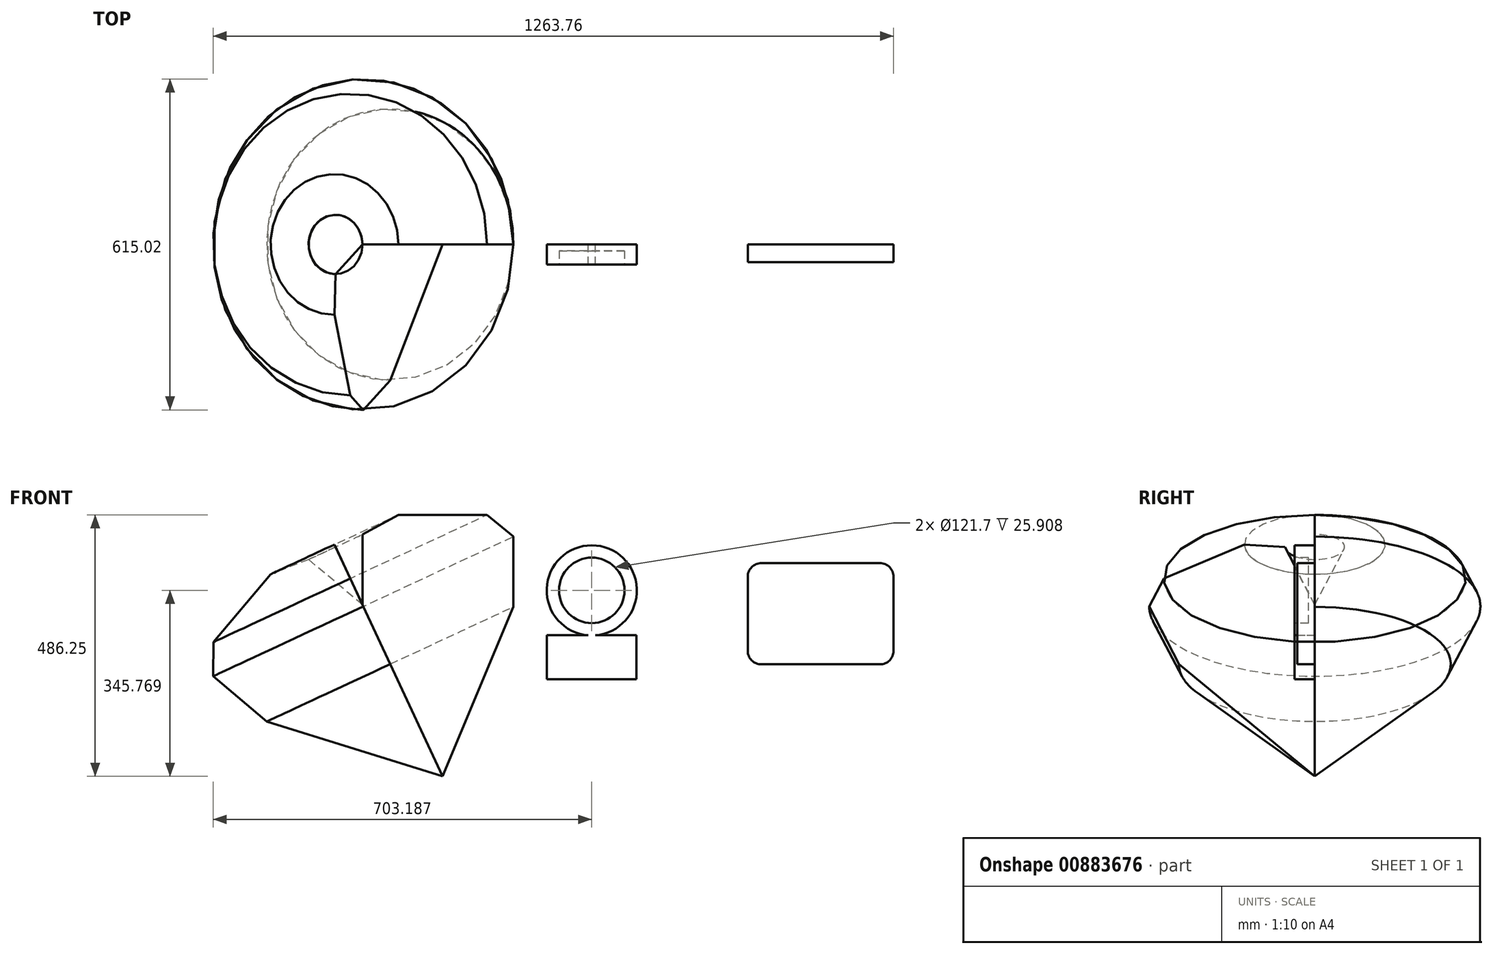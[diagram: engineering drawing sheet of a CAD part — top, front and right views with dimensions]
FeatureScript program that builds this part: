
annotation { "Feature Type Name" : "Feature", "Feature Type Description" : "" }
export const myFeature = defineFeature(function(context is Context, id is Id, definition is map)
    precondition{}
    {
        {
            var Q0;
            Q0=qCreatedBy(makeId("Front.planeOp"),FACE);
            var sketch = newSketch(context, id + "F0", { "sketchPlane" : qUnion([Q0])});
            skLineSegment(sketch, "E0.bottom", {"start": v(-289.04, 54.01) * mm, "end": v(-122.87, 54.01) * mm});
            skLineSegment(sketch, "E0.top", {"start": v(-289.04, -27.36) * mm, "end": v(-122.87, -27.36) * mm});
            skLineSegment(sketch, "E0.left", {"start": v(-289.04, 54.01) * mm, "end": v(-289.04, -27.36) * mm});
            skLineSegment(sketch, "E0.right", {"start": v(-122.87, 54.01) * mm, "end": v(-122.87, -27.36) * mm});
            skCircle(sketch, "E1", {"center": v(-205.51, 137.54) * mm, "radius": 83.78 * mm});
            skCircle(sketch, "E2", {"center": v(-205.51, 137.54) * mm, "radius": 83.53 * mm});
            skSolve(sketch);
        }
        {
            var Q0;
            Q0=makeQuery(id+"F0.imprint","IMPRINT",FACE,{"disambiguationData":[TD([[makeQuery(id+"F0.imprint","IMPRINT",EDGE,{"derivedFrom":sQuery(id+"F0.wireOp",EDGE,"E0.top")}),1.0]])]});
            var Q1;
            Q1=makeQuery(id+"F0.imprint","IMPRINT",FACE,{"disambiguationData":[TD([[makeQuery(id+"F0.imprint","IMPRINT",EDGE,{"derivedFrom":sQuery(id+"F0.wireOp",EDGE,"E2")}),1.0]])]});
            var Q2;
            {var subQ3=sQuery(id+"F0.wireOp",EDGE,"E2");Q2=makeQuery(id+"F0.imprint","IMPRINT",FACE,{"disambiguationData":[TD([[makeQuery(id+"F0.imprint","IMPRINT",EDGE,{"derivedFrom":subQ3}),-1.0]])]});}
            var Q3;
            {var subQ0=sQuery(id+"F0.wireOp",EDGE,"E1");var subQ1=sQuery(id+"F0.wireOp",EDGE,"E0.bottom");var subQ2=makeQuery(id+"F0.imprint","INTERSECT",VERTEX,{"disambiguationData":[OD(0.0)],"derivedFrom":[subQ1,subQ0]});Q3=makeQuery(id+"F0.imprint","IMPRINT",FACE,{"disambiguationData":[TD([[makeQuery(id+"F0.imprint","IMPRINT",EDGE,{"disambiguationData":[TD([[subQ2,-1.0]])],"derivedFrom":subQ1}),-1.0]])]});}
            extrude(context, id + "F1", {"entities" : qUnion([Q0, Q1, Q2, Q3]), "surfaceOperationType" : NewSurfaceOperationType.ADD, "depth" : 37.6 * mm, "offsetDistance" : 25.4 * mm});
        }
        {
            var Q0;
            Q0=makeQuery(id+"F1.opExtrude","CAP_FACE",FACE,{"disambiguationData":[OSD([sQuery(id+"F0.wireOp",EDGE,"E0.bottom"),sQuery(id+"F0.wireOp",EDGE,"E0.top"),sQuery(id+"F0.wireOp",EDGE,"E0.left"),sQuery(id+"F0.wireOp",EDGE,"E0.right"),sQuery(id+"F0.wireOp",EDGE,"E1")])],"isStart":false});
            var sketch = newSketch(context, id + "F2", { "sketchPlane" : qUnion([Q0])});
            skCircle(sketch, "E3", {"center": v(-205.51, 137.54) * mm, "radius": 60.85 * mm});
            skSolve(sketch);
        }
        {
            var Q0;
            Q0=makeQuery(id+"F2.imprint","IMPRINT",FACE,{"disambiguationData":[TD([[makeQuery(id+"F2.imprint","IMPRINT",EDGE,{"derivedFrom":sQuery(id+"F2.wireOp",EDGE,"E3")}),1.0]])]});
            extrude(context, id + "F3", {"entities" : qUnion([Q0]), "operationType" : NewBodyOperationType.REMOVE, "oppositeDirection" : true, "depth" : 25.9 * mm, "offsetDistance" : 25.4 * mm});
        }
        {
            var Q0;
            Q0=qCreatedBy(makeId("Front.planeOp"),FACE);
            var sketch = newSketch(context, id + "F4", { "sketchPlane" : qUnion([Q0])});
            skLineSegment(sketch, "E4.bottom", {"start": v(109.57, 188.23) * mm, "end": v(329.66, 188.23) * mm});
            skLineSegment(sketch, "E4.top", {"start": v(109.57, 0) * mm, "end": v(329.66, 0) * mm});
            skLineSegment(sketch, "E4.left", {"start": v(84.17, 162.83) * mm, "end": v(84.17, 25.4) * mm});
            skLineSegment(sketch, "E4.right", {"start": v(355.06, 162.83) * mm, "end": v(355.06, 25.4) * mm});
            skPoint(sketch, "E5.visualSharp", {"position": v(84.17, 188.23) * mm});
            skArc(sketch, "E5.filletArc", {"start": v(109.57, 188.23) * mm, "mid": v(91.6, 180.79) * mm, "end": v(84.17, 162.83) * mm});
            skPoint(sketch, "E6.visualSharp", {"position": v(355.06, 188.23) * mm});
            skArc(sketch, "E6.filletArc", {"start": v(355.06, 162.83) * mm, "mid": v(347.62, 180.79) * mm, "end": v(329.66, 188.23) * mm});
            skPoint(sketch, "E7.visualSharp", {"position": v(355.06, 0) * mm});
            skArc(sketch, "E7.filletArc", {"start": v(329.66, 0) * mm, "mid": v(347.62, 7.44) * mm, "end": v(355.06, 25.4) * mm});
            skPoint(sketch, "E8.visualSharp", {"position": v(84.17, 0) * mm});
            skArc(sketch, "E8.filletArc", {"start": v(84.17, 25.4) * mm, "mid": v(91.6, 7.44) * mm, "end": v(109.57, 0) * mm});
            skSolve(sketch);
        }
        {
            var Q0;
            Q0=makeQuery(id+"F4.imprint","IMPRINT",FACE,{"disambiguationData":[TD([[makeQuery(id+"F4.imprint","IMPRINT",EDGE,{"derivedFrom":sQuery(id+"F4.wireOp",EDGE,"E4.bottom")}),-1.0]])]});
            extrude(context, id + "F5", {"entities" : qUnion([Q0]), "depth" : 32.77 * mm, "offsetDistance" : 25.4 * mm});
        }
        {
            var Q0;
            Q0=qCreatedBy(makeId("Front.planeOp"),FACE);
            var sketch = newSketch(context, id + "F6", { "sketchPlane" : qUnion([Q0])});
            skLineSegment(sketch, "E9", {"start": v(-631.34, 110.72) * mm, "end": v(-631.34, 241.52) * mm});
            skLineSegment(sketch, "E10", {"start": v(-631.34, 241.52) * mm, "end": v(-564.87, 278.02) * mm});
            skLineSegment(sketch, "E11", {"start": v(-564.87, 278.02) * mm, "end": v(-399.9, 278.02) * mm});
            skLineSegment(sketch, "E12", {"start": v(-399.9, 278.02) * mm, "end": v(-351.16, 237.5) * mm});
            skLineSegment(sketch, "E13", {"start": v(-351.16, 237.5) * mm, "end": v(-351.16, 106.96) * mm});
            skLineSegment(sketch, "E14", {"start": v(-351.16, 106.96) * mm, "end": v(-482.82, -208.23) * mm});
            skLineSegment(sketch, "E15", {"start": v(-482.82, -208.23) * mm, "end": v(-631.34, 110.72) * mm});
            skSolve(sketch);
        }
        {
            var Q0;
            Q0=makeQuery(id+"F6.imprint","IMPRINT",FACE,{"disambiguationData":[TD([[makeQuery(id+"F6.imprint","IMPRINT",EDGE,{"derivedFrom":sQuery(id+"F6.wireOp",EDGE,"E9")}),-1.0]])]});
            var Q1;
            Q1=sQuery(id+"F6.wireOp",EDGE,"E15");
            revolve(context, id + "F7", {"surfaceOperationType" : NewSurfaceOperationType.NEW, "entities" : qUnion([Q0]), "axis" : qUnion([Q1]), "revolveType" : RevolveType.ONE_DIRECTION, "angle" : 270 * degree});
        }
    });
